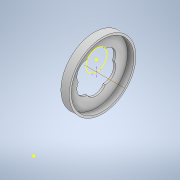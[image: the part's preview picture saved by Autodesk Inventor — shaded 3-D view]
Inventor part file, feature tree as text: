
AUTODESK INVENTOR PART (.ipt)
format: ipt  version: 2020 (Build 240168000, 168)  size: 205,312 bytes
history: native  units: in
note: dims shown in document units (in); Inventor stores cm internally (conversion verified against a paired STEP export)
features: sketch x10, extrude x8, fillet x2, hole x1, other x1, pattern_circular x1
ambient origin geometry x8: Origin, YZ Plane, XZ Plane, XY Plane, X Axis, Y Axis, Z Axis, Center Point
bodies: Solid1 (feature_tree)
feature tree (23):
  extrude  "Extrusion1"  Depth=3.0in
  extrude  "Extrusion2"  Depth=0.5in
  extrude  "Extrusion3"  Depth=2.0in
  fillet  "Fillet1"  Radius=1.7in
  sketch  "Sketch6"  dims[d10=1.5in d11=0.6in d12=0.0in]
  fillet  "Fillet2"  Radius=1.0in
  hole  "Hole1"  [1 undecoded]
  extrude  "Extrusion5"  Depth=0.25in
  extrude  "Extrusion8"  Depth=0.25in
  sketch  "Sketch13"  dims[d23=0.2in d24=0.75in d25=0.4in d26=0.15in d27=0.5635in d28=1.0in d29=0.8108in]
  other  "Work Axis3"
  pattern_circular  "Circular Pattern3"  [2 undecoded]
  extrude  "Extrusion10"  Depth=0.15in TaperAngle=0.0deg
  extrude  "Extrusion11"  Depth=0.15in TaperAngle=360.0deg
  extrude  "Extrusion12"  Depth=0.15in TaperAngle=0.0deg
  sketch  "Sketch1"  dims[d0=0.8in d1=3.0in]
  sketch  "Sketch2"  dims[d2=0.3in d3=0.0in d4=0.5in]
  sketch  "Sketch3"  dims[d5=0.8in d6=2.0in d7=1.7in d8=0.0in d9=1.0in]
  sketch  "Sketch7"  dims[d19=1.0in d20=0.25in]
  sketch  "Sketch10"  dims[d21=0.25in d22=1.0in]
  sketch  "Sketch14"  dims[d30=0.4in]
  sketch  "Sketch15"  dims[d31=0.4in]
  sketch  "Sketch16"  dims[d32=0.6in d33=0.0in d65=0.25in d66=1.0in d67=0.0in d76=2.3622in d77=360.0deg d79=2.0in d80=0.0in d81=0.45in d82=0.0in d83=0.15in d84=0.0in d85=0.62in d86=120.0deg d87=0.62in d88=60.0deg d89=0.13in d90=0.13in]
note: 3 required parameter values undecoded (feature->parameter linkage not recoverable at this tier; creation-order binding heuristic only, values carry confidence <= 0.55)
